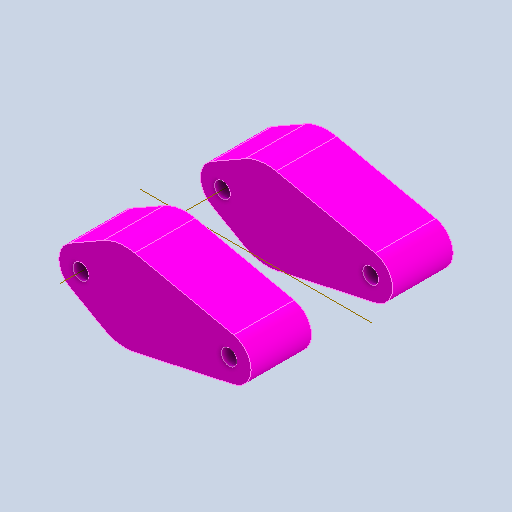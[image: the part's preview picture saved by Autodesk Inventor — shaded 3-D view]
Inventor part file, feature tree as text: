
AUTODESK INVENTOR PART (.ipt)
format: ipt  version: 2025 (Build 290162000, 162)  size: 177,152 bytes
history: native  units: mm
features: sketch x6, hole x4, other x2, extrude x2, plane x1, mirror x1
ambient origin geometry x8: Origin, YZ Plane, XZ Plane, XY Plane, X Axis, Y Axis, Z Axis, Center Point
bodies: Body1 (feature_tree)
feature tree (16):
  parser-record x1  (decoder bookkeeping rows leaked as tree rows — omitted from the tree; the rows remain in map.json)
  other  "實體1"
  plane  "工作平面1"
  extrude  "擠出1"  Depth=172.0mm
  extrude  "擠出2"  Depth=252.3048mm
  hole  "孔1"  [1 undecoded]
  hole  "孔2"  [1 undecoded]
  hole  "孔4"  [1 undecoded]
  hole  "孔5"  [1 undecoded]
  mirror  "鏡射1"
  sketch  "草圖1"
  sketch  "草圖2"
  sketch  "草圖3"
  sketch  "草圖4"
  sketch  "草圖6"
  sketch  "草圖7"
note: 4 required parameter values undecoded (feature->parameter linkage not recoverable at this tier; creation-order binding heuristic only, values carry confidence <= 0.55)
note: 1 file-system path scrubbed to <path> (originals preserved in map.json)
